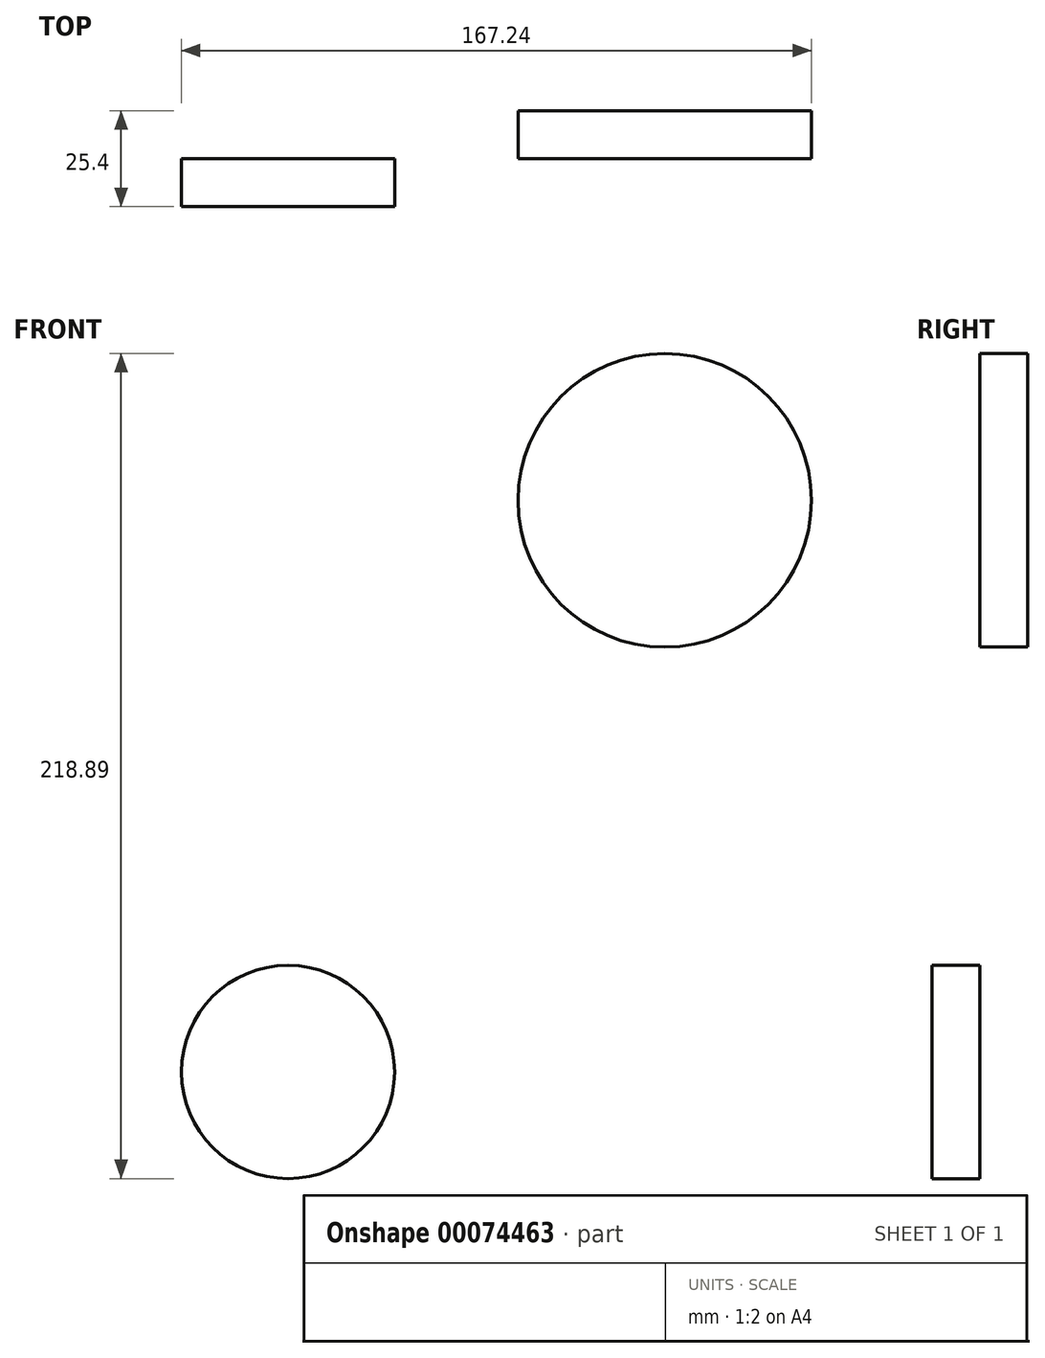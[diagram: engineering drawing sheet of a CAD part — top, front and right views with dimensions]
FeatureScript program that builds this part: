
annotation { "Feature Type Name" : "Feature", "Feature Type Description" : "" }
export const myFeature = defineFeature(function(context is Context, id is Id, definition is map)
    precondition{}
    {
        {
            var Q0;
            Q0=qCreatedBy(makeId("Front.planeOp"),FACE);
            var sketch = newSketch(context, id + "F0", { "sketchPlane" : qUnion([Q0])});
            skCircle(sketch, "E0", {"center": v(0, 0) * mm, "radius": 28.29 * mm});
            skSolve(sketch);
        }
        {
            var Q0;
            Q0=qCreatedBy(makeId("Front.planeOp"),FACE);
            var sketch = newSketch(context, id + "F1", { "sketchPlane" : qUnion([Q0])});
            skCircle(sketch, "E1", {"center": v(100, 151.65) * mm, "radius": 38.95 * mm});
            skSolve(sketch);
        }
        {
            var Q0;
            Q0=makeQuery(id+"F0.imprint","IMPRINT",FACE,{"disambiguationData":[TD([[makeQuery(id+"F0.imprint","IMPRINT",EDGE,{"derivedFrom":sQuery(id+"F0.wireOp",EDGE,"E0")}),1.0]])]});
            extrude(context, id + "F2", {"entities" : qUnion([Q0]), "depth" : 12.7 * mm});
        }
        {
            var Q0;
            Q0=makeQuery(id+"F1.imprint","IMPRINT",FACE,{"disambiguationData":[TD([[makeQuery(id+"F1.imprint","IMPRINT",EDGE,{"derivedFrom":sQuery(id+"F1.wireOp",EDGE,"E1")}),1.0]])]});
            extrude(context, id + "F3", {"entities" : qUnion([Q0]), "oppositeDirection" : true, "depth" : 12.7 * mm});
        }
    });
